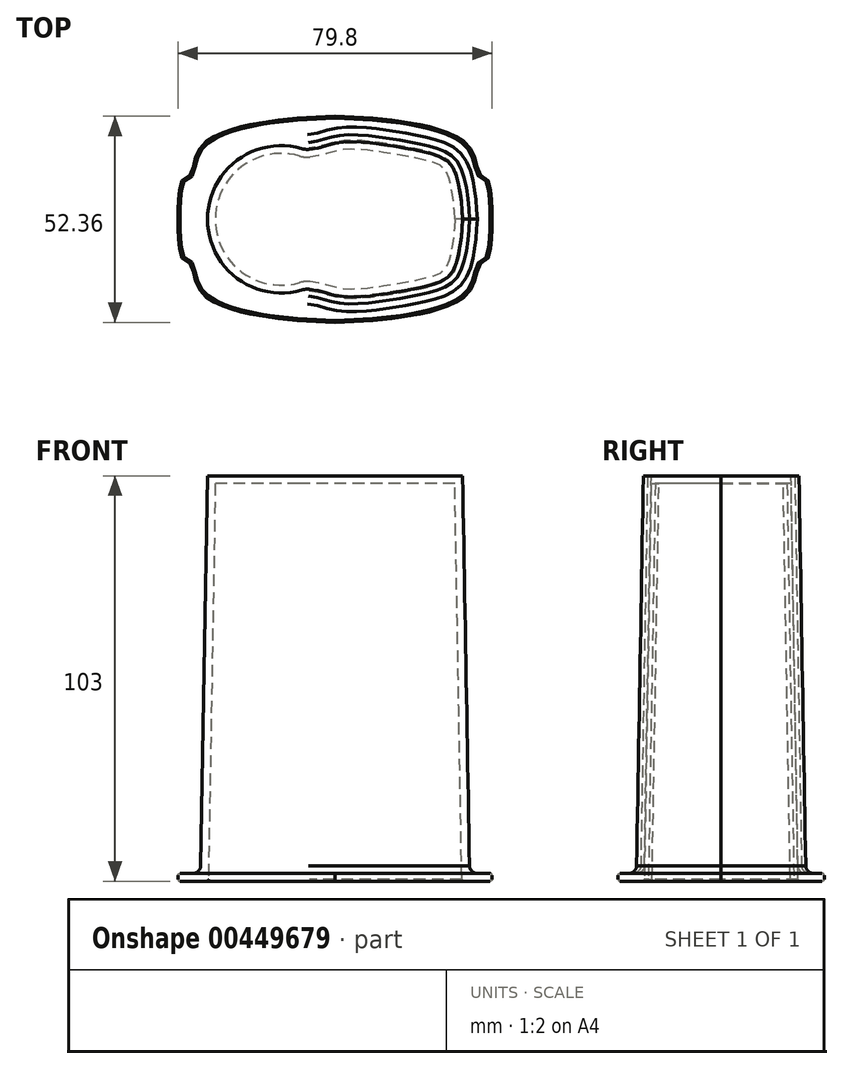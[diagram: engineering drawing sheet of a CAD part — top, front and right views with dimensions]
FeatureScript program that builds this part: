
annotation { "Feature Type Name" : "Feature", "Feature Type Description" : "" }
export const myFeature = defineFeature(function(context is Context, id is Id, definition is map)
    precondition{}
    {
        {
            var Q0;
            Q0=qCreatedBy(makeId("Top.planeOp"),FACE);
            var sketch = newSketch(context, id + "F0", { "sketchPlane" : qUnion([Q0])});
            skLineSegment(sketch, "E0", {"start": v(0, 26.18) * mm, "end": v(0, -26.18) * mm, "construction": true});
            skLineSegment(sketch, "E1", {"start": v(-36.75, 0) * mm, "end": v(36.75, 0) * mm, "construction": true});
            skSolve(sketch);
        }
        {
            var Q0;
            Q0=qCreatedBy(makeId("Top.planeOp"),FACE);
            cPlane(context, id + "F1", {"entities" : qUnion([Q0]), "cplaneType" : CPlaneType.OFFSET, "offset" : 103 * mm, "width" : 150 * mm, "height" : 150 * mm});
        }
        {
            var Q0;
            Q0=qCreatedBy(id+"F1.planeOp",FACE);
            var sketch = newSketch(context, id + "F2", { "sketchPlane" : qUnion([Q0])});
            skLineSegment(sketch, "E2", {"start": v(0, 19.93) * mm, "end": v(0, -19.93) * mm, "construction": true});
            skLineSegment(sketch, "E3", {"start": v(-32.4, 0) * mm, "end": v(32.4, 0) * mm, "construction": true});
            skSolve(sketch);
        }
        {
            var Q0;
            Q0=qCreatedBy(makeId("Top.planeOp"),FACE);
            var sketch = newSketch(context, id + "F3", { "sketchPlane" : qUnion([Q0])});
            skFitSpline(sketch, "E4", {"points": [v(-39.9, 0) * mm, v(-38.53, 10.31) * mm, v(-36.7, 11.44) * mm, v(-33.5, 18.99) * mm, v(0, 26.18) * mm], "startDerivative": vector(0.34, 57.54) * mm, "endDerivative": vector(72.62, 1.2) * mm});
            skLineSegment(sketch, "E5", {"start": v(0, 0) * mm, "end": v(0, 26.18) * mm, "construction": true});
            skFitSpline(sketch, "E6.MirrorCS", {"points": [v(39.9, 0) * mm, v(38.53, 10.31) * mm, v(36.7, 11.44) * mm, v(33.5, 18.99) * mm, v(0, 26.18) * mm], "startDerivative": vector(-0.34, 57.54) * mm, "endDerivative": vector(-72.62, 1.2) * mm});
            skFitSpline(sketch, "E7.MirrorCS", {"points": [v(39.9, 0) * mm, v(38.53, -10.31) * mm, v(36.7, -11.44) * mm, v(33.5, -18.99) * mm, v(0, -26.18) * mm], "startDerivative": vector(-0.34, -57.54) * mm, "endDerivative": vector(-72.62, -1.2) * mm});
            skFitSpline(sketch, "E8.MirrorCS", {"points": [v(-39.9, 0) * mm, v(-38.53, -10.31) * mm, v(-36.7, -11.44) * mm, v(-33.5, -18.99) * mm, v(0, -26.18) * mm], "startDerivative": vector(0.34, -57.54) * mm, "endDerivative": vector(72.62, -1.2) * mm});
            skSolve(sketch);
        }
        {
            var Q0;
            Q0=qCreatedBy(id+"F1.planeOp",FACE);
            var sketch = newSketch(context, id + "F4", { "sketchPlane" : qUnion([Q0])});
            skArc(sketch, "E9", {"start": v(-8.48, 17.96) * mm, "mid": v(-32.4, 0) * mm, "end": v(-8.48, -17.96) * mm});
            skFitSpline(sketch, "E10", {"points": [v(32.4, 0) * mm, v(30.23, 12.69) * mm, v(26.09, 16.12) * mm, v(14.2, 18.7) * mm, v(1.4, 19.58) * mm, v(-7.65, 17.7) * mm], "startDerivative": vector(-2.91, 56.6) * mm, "endDerivative": vector(-65.15, -3.88) * mm});
            skFitSpline(sketch, "E11.MirrorCS", {"points": [v(32.4, 0) * mm, v(30.23, -12.69) * mm, v(26.09, -16.12) * mm, v(14.2, -18.7) * mm, v(1.4, -19.58) * mm, v(-7.65, -17.7) * mm], "startDerivative": vector(-2.91, -56.6) * mm, "endDerivative": vector(-65.15, 3.88) * mm});
            skArc(sketch, "E12.filletArc", {"start": v(-8.48, 17.96) * mm, "mid": v(-7.52, 17.78) * mm, "end": v(-6.54, 17.79) * mm});
            skArc(sketch, "E13.filletArc", {"start": v(-6.54, -17.79) * mm, "mid": v(-7.52, -17.78) * mm, "end": v(-8.48, -17.96) * mm});
            skSolve(sketch);
        }
        {
            var Q0;
            Q0 = qSketchRegion(id + "F4", true);
            var Q1;
            Q1=sQuery(id+"F3.wireOp",VERTEX,"E5.start");
            extrude(context, id + "F5", {"entities" : qUnion([Q0]), "endBound" : BoundingType.UP_TO_VERTEX, "oppositeDirection" : true, "depth" : 75.7 * mm, "endBoundEntityVertex" : qUnion([Q1]), "offsetDistance" : 25 * mm, "hasDraft" : true, "draftAngle" : 1 * degree});
        }
        {
            var Q0;
            Q0 = qSketchRegion(id + "F3", true);
            extrude(context, id + "F6", {"entities" : qUnion([Q0]), "operationType" : NewBodyOperationType.ADD, "depth" : 2 * mm, "offsetDistance" : 25 * mm});
        }
        {
            var Q0;
            Q0=makeQuery(id+"F6.boolean.opBoolean","MERGE",FACE,{"derivedFrom":[makeQuery(id+"F5.opExtrude","CAP_FACE",FACE,{"disambiguationData":[OSD([sQuery(id+"F4.wireOp",EDGE,"E9"),sQuery(id+"F4.wireOp",EDGE,"E10"),sQuery(id+"F4.wireOp",EDGE,"E11.MirrorCS"),sQuery(id+"F4.wireOp",EDGE,"E12.filletArc"),sQuery(id+"F4.wireOp",EDGE,"E13.filletArc")])],"isStart":false}),makeQuery(id+"F6.opExtrude","CAP_FACE",FACE,{"disambiguationData":[OSD([sQuery(id+"F3.wireOp",EDGE,"E4"),sQuery(id+"F3.wireOp",EDGE,"E6.MirrorCS"),sQuery(id+"F3.wireOp",EDGE,"E7.MirrorCS"),sQuery(id+"F3.wireOp",EDGE,"E8.MirrorCS")])],"isStart":true})]});
            shell(context, id + "F7", {"entities" : qUnion([Q0]), "thickness" : 2 * mm});
        }
        {
            var Q0;
            Q0=makeQuery(id+"F6.boolean.opBoolean","INTERSECT",EDGE,{"derivedFrom":[makeQuery(id+"F5.opExtrude","SWEPT_FACE",FACE,{"disambiguationData":[OSD([sQuery(id+"F4.wireOp",EDGE,"E9")])]}),makeQuery(id+"F6.opExtrude","CAP_FACE",FACE,{"disambiguationData":[OSD([sQuery(id+"F3.wireOp",EDGE,"E4"),sQuery(id+"F3.wireOp",EDGE,"E6.MirrorCS"),sQuery(id+"F3.wireOp",EDGE,"E7.MirrorCS"),sQuery(id+"F3.wireOp",EDGE,"E8.MirrorCS")])],"isStart":false})]});
            fillet(context, id + "F8", {"entities" : qUnion([Q0]), "radius" : 2 * mm, "tangentPropagation" : true, "allowEdgeOverflow" : false});
        }
        {
            var Q0;
            Q0=makeQuery(id+"F6.boolean.opBoolean","MERGE",FACE,{"derivedFrom":[makeQuery(id+"F5.opExtrude","CAP_FACE",FACE,{"disambiguationData":[OSD([sQuery(id+"F4.wireOp",EDGE,"E9"),sQuery(id+"F4.wireOp",EDGE,"E10"),sQuery(id+"F4.wireOp",EDGE,"E11.MirrorCS"),sQuery(id+"F4.wireOp",EDGE,"E12.filletArc"),sQuery(id+"F4.wireOp",EDGE,"E13.filletArc")])],"isStart":false}),makeQuery(id+"F6.opExtrude","CAP_FACE",FACE,{"disambiguationData":[OSD([sQuery(id+"F3.wireOp",EDGE,"E4"),sQuery(id+"F3.wireOp",EDGE,"E6.MirrorCS"),sQuery(id+"F3.wireOp",EDGE,"E7.MirrorCS"),sQuery(id+"F3.wireOp",EDGE,"E8.MirrorCS")])],"isStart":true})]});
            var Q1;
            Q1=makeQuery(id+"F6.opExtrude","CAP_EDGE",EDGE,{"disambiguationData":[OSD([sQuery(id+"F3.wireOp",EDGE,"E7.MirrorCS")])],"isStart":false});
            var Q2;
            Q2=makeQuery(id+"F6.opExtrude","CAP_EDGE",EDGE,{"disambiguationData":[OSD([sQuery(id+"F3.wireOp",EDGE,"E6.MirrorCS")])],"isStart":false});
            var Q3;
            Q3=makeQuery(id+"F6.opExtrude","CAP_EDGE",EDGE,{"disambiguationData":[OSD([sQuery(id+"F3.wireOp",EDGE,"E4")])],"isStart":false});
            var Q4;
            Q4=makeQuery(id+"F6.opExtrude","CAP_EDGE",EDGE,{"disambiguationData":[OSD([sQuery(id+"F3.wireOp",EDGE,"E8.MirrorCS")])],"isStart":false});
            fillet(context, id + "F9", {"entities" : qUnion([Q0, Q1, Q2, Q3, Q4]), "radius" : 0.51 * mm, "tangentPropagation" : true, "allowEdgeOverflow" : false});
        }
    });
